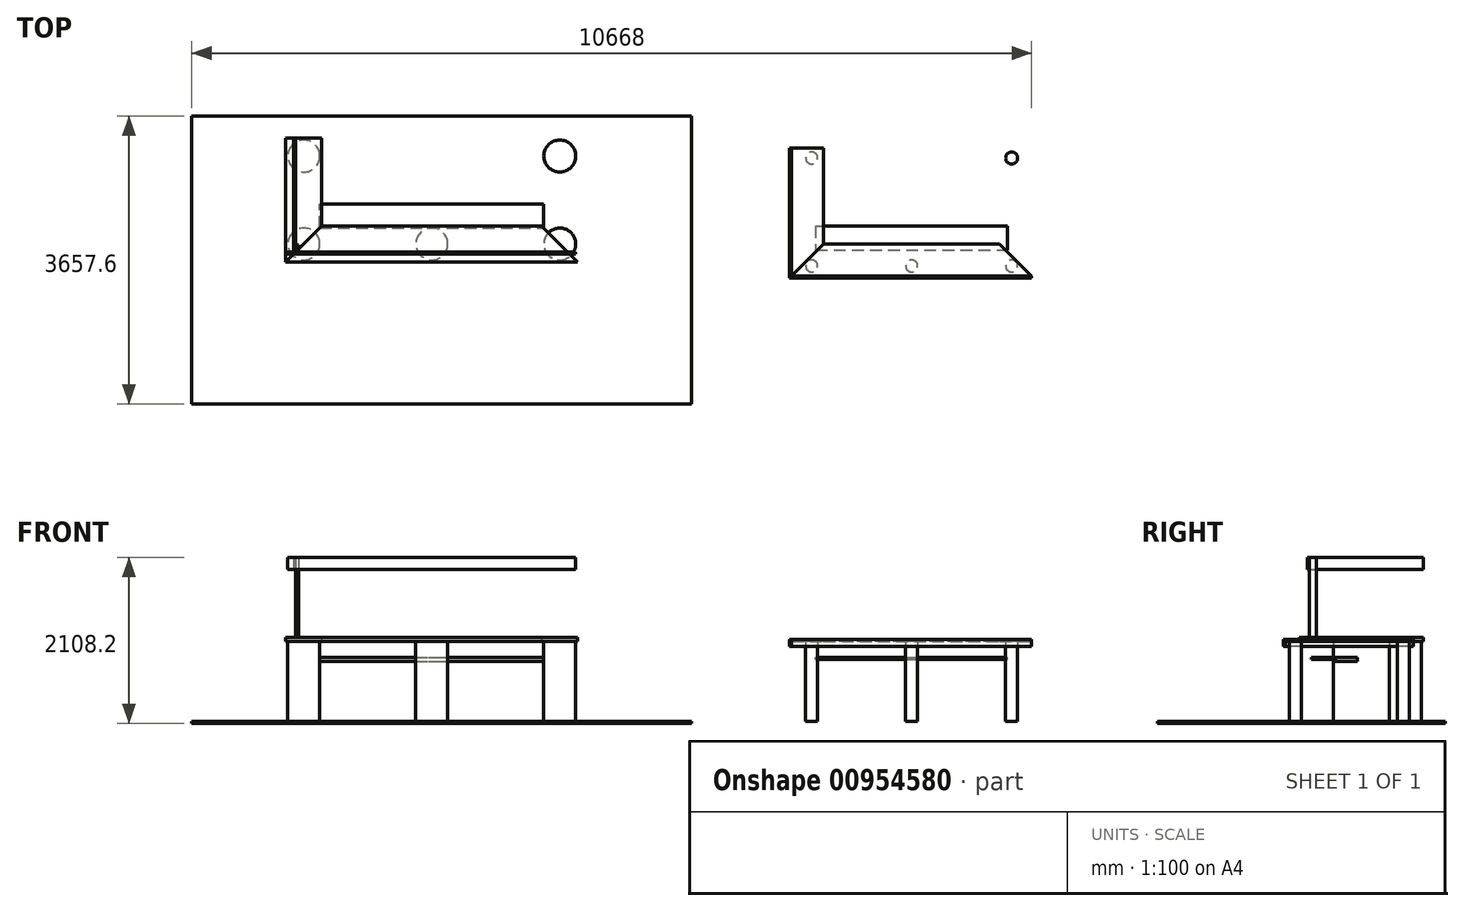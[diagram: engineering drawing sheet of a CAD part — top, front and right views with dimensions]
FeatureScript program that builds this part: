
annotation { "Feature Type Name" : "Feature", "Feature Type Description" : "" }
export const myFeature = defineFeature(function(context is Context, id is Id, definition is map)
    precondition{}
    {
        {
            var Q0;
            Q0=qCreatedBy(makeId("Top.planeOp"),FACE);
            var sketch = newSketch(context, id + "F0", { "sketchPlane" : qUnion([Q0])});
            skLineSegment(sketch, "E0.bottom", {"start": v(-3048, 1828.8) * mm, "end": v(3302, 1828.8) * mm});
            skLineSegment(sketch, "E0.top", {"start": v(-3048, -1828.8) * mm, "end": v(3302, -1828.8) * mm});
            skLineSegment(sketch, "E0.left", {"start": v(-3048, 1828.8) * mm, "end": v(-3048, -1828.8) * mm});
            skLineSegment(sketch, "E0.right", {"start": v(3302, 1828.8) * mm, "end": v(3302, -1828.8) * mm});
            skLineSegment(sketch, "E1", {"start": v(-3048, 0) * mm, "end": v(0, 0) * mm, "construction": true});
            skSolve(sketch);
        }
        {
            var Q0;
            Q0=makeQuery(id+"F0.imprint","IMPRINT",FACE,{"disambiguationData":[TD([[makeQuery(id+"F0.imprint","IMPRINT",EDGE,{"derivedFrom":sQuery(id+"F0.wireOp",EDGE,"E0.bottom")}),-1.0]])]});
            extrude(context, id + "F1", {"entities" : qUnion([Q0]), "oppositeDirection" : true, "depth" : 25.4 * mm, "offsetDistance" : 25.4 * mm});
        }
        {
            var Q0;
            Q0=qCreatedBy(makeId("Top.planeOp"),FACE);
            var sketch = newSketch(context, id + "F2", { "sketchPlane" : qUnion([Q0])});
            skLineSegment(sketch, "E2", {"start": v(0, 0) * mm, "end": v(1625.6, 0) * mm, "construction": true});
            skLineSegment(sketch, "E3", {"start": v(0, 0) * mm, "end": v(-1625.6, 0) * mm, "construction": true});
            skCircle(sketch, "E4", {"center": v(0, 203.2) * mm, "radius": 203.2 * mm});
            skCircle(sketch, "E5", {"center": v(1625.6, 203.2) * mm, "radius": 203.2 * mm});
            skCircle(sketch, "E6", {"center": v(-1625.6, 203.2) * mm, "radius": 203.2 * mm});
            skLineSegment(sketch, "E7", {"start": v(-1625.6, 0) * mm, "end": v(-1625.6, 203.2) * mm, "construction": true});
            skLineSegment(sketch, "E8", {"start": v(0, 203.2) * mm, "end": v(0, 0) * mm, "construction": true});
            skLineSegment(sketch, "E9", {"start": v(1625.6, 203.2) * mm, "end": v(1625.6, 0) * mm, "construction": true});
            skLineSegment(sketch, "E10", {"start": v(-1422.4, 203.2) * mm, "end": v(-203.2, 203.2) * mm, "construction": true});
            skLineSegment(sketch, "E11", {"start": v(203.2, 203.2) * mm, "end": v(1422.4, 203.2) * mm, "construction": true});
            skCircle(sketch, "E12", {"center": v(-1625.6, 1320.8) * mm, "radius": 203.2 * mm});
            skCircle(sketch, "E13", {"center": v(1625.6, 1320.8) * mm, "radius": 203.2 * mm});
            skLineSegment(sketch, "E14", {"start": v(-1625.6, 203.2) * mm, "end": v(-1625.6, 1320.8) * mm, "construction": true});
            skLineSegment(sketch, "E15", {"start": v(1625.6, 203.2) * mm, "end": v(1625.6, 1320.8) * mm, "construction": true});
            skLineSegment(sketch, "E16", {"start": v(-1625.6, 1524) * mm, "end": v(1625.6, 1524) * mm, "construction": true});
            skSolve(sketch);
        }
        {
            var Q0;
            Q0 = qSketchRegion(id + "F2", true);
            extrude(context, id + "F3", {"entities" : qUnion([Q0]), "depth" : 1016 * mm, "offsetDistance" : 25.4 * mm});
        }
        {
            var Q0;
            Q0=qCreatedBy(makeId("Top.planeOp"),FACE);
            cPlane(context, id + "F4", {"entities" : qUnion([Q0]), "cplaneType" : CPlaneType.OFFSET, "offset" : 1016 * mm, "width" : 152.4 * mm, "height" : 152.4 * mm});
        }
        {
            var Q0;
            Q0=qCreatedBy(id+"F4.planeOp",FACE);
            var sketch = newSketch(context, id + "F5", { "sketchPlane" : qUnion([Q0])});
            skLineSegment(sketch, "E17", {"start": v(-1854.2, -25.4) * mm, "end": v(-1397, 431.8) * mm});
            skLineSegment(sketch, "E18", {"start": v(-1397, 431.8) * mm, "end": v(1397, 431.8) * mm});
            skLineSegment(sketch, "E19", {"start": v(1397, 431.8) * mm, "end": v(1854.2, -25.4) * mm});
            skLineSegment(sketch, "E20", {"start": v(1854.2, -25.4) * mm, "end": v(-1854.2, -25.4) * mm});
            skLineSegment(sketch, "E21", {"start": v(0, 0) * mm, "end": v(0, -25.4) * mm, "construction": true});
            skSolve(sketch);
        }
        {
            var Q0;
            Q0=makeQuery(id+"F5.imprint","IMPRINT",FACE,{"disambiguationData":[TD([[makeQuery(id+"F5.imprint","IMPRINT",EDGE,{"derivedFrom":sQuery(id+"F5.wireOp",EDGE,"E17")}),-1.0]])]});
            extrude(context, id + "F6", {"entities" : qUnion([Q0]), "depth" : 50.8 * mm, "offsetDistance" : 25.4 * mm});
        }
        {
            var Q0;
            Q0=qCreatedBy(id+"F4.planeOp",FACE);
            var sketch = newSketch(context, id + "F7", { "sketchPlane" : qUnion([Q0])});
            skLineSegment(sketch, "E22", {"start": v(-1397, 431.8) * mm, "end": v(-1397, 1549.4) * mm});
            skLineSegment(sketch, "E23", {"start": v(-1397, 1549.4) * mm, "end": v(-1854.2, 1549.4) * mm});
            skLineSegment(sketch, "E24", {"start": v(-1854.2, 1549.4) * mm, "end": v(-1854.2, -25.4) * mm});
            skLineSegment(sketch, "E25", {"start": v(-1854.2, -25.4) * mm, "end": v(-1397, 431.8) * mm});
            skLineSegment(sketch, "E26", {"start": v(0, 0) * mm, "end": v(0, -25.4) * mm, "construction": true});
            skLineSegment(sketch, "E27", {"start": v(0, -25.4) * mm, "end": v(-1854.2, -25.4) * mm, "construction": true});
            skSolve(sketch);
        }
        {
            var Q0;
            Q0 = qSketchRegion(id + "F7", true);
            extrude(context, id + "F8", {"entities" : qUnion([Q0]), "depth" : 50.8 * mm, "offsetDistance" : 25.4 * mm});
        }
        {
            var Q0;
            Q0=qCreatedBy(makeId("Top.planeOp"),FACE);
            cPlane(context, id + "F9", {"entities" : qUnion([Q0]), "cplaneType" : CPlaneType.OFFSET, "offset" : 812.8 * mm, "width" : 152.4 * mm, "height" : 152.4 * mm});
        }
        {
            var Q0;
            Q0=qCreatedBy(id+"F9.planeOp",FACE);
            var sketch = newSketch(context, id + "F10", { "sketchPlane" : qUnion([Q0])});
            skLineSegment(sketch, "E28.bottom", {"start": v(-1422.4, 406.4) * mm, "end": v(1422.4, 406.4) * mm});
            skLineSegment(sketch, "E28.top", {"start": v(-1422.4, 711.2) * mm, "end": v(1422.4, 711.2) * mm});
            skLineSegment(sketch, "E28.left", {"start": v(-1422.4, 406.4) * mm, "end": v(-1422.4, 711.2) * mm});
            skLineSegment(sketch, "E28.right", {"start": v(1422.4, 406.4) * mm, "end": v(1422.4, 711.2) * mm});
            skLineSegment(sketch, "E29", {"start": v(0, 0) * mm, "end": v(0, 406.4) * mm, "construction": true});
            skSolve(sketch);
        }
        {
            var Q0;
            Q0 = qSketchRegion(id + "F10", true);
            extrude(context, id + "F11", {"entities" : qUnion([Q0]), "operationType" : NewBodyOperationType.ADD, "oppositeDirection" : true, "depth" : 50.8 * mm, "offsetDistance" : 25.4 * mm});
        }
        {
            var Q0;
            Q0=makeQuery(id+"F6.opExtrude","CAP_FACE",FACE,{"disambiguationData":[OSD([sQuery(id+"F5.wireOp",EDGE,"E17"),sQuery(id+"F5.wireOp",EDGE,"E18"),sQuery(id+"F5.wireOp",EDGE,"E19"),sQuery(id+"F5.wireOp",EDGE,"E20")])],"isStart":false});
            cPlane(context, id + "F12", {"entities" : qUnion([Q0]), "cplaneType" : CPlaneType.OFFSET, "offset" : 0 * mm, "width" : 152.4 * mm, "height" : 152.4 * mm});
        }
        {
            var Q0;
            Q0=qCreatedBy(id+"F12.planeOp",FACE);
            var sketch = newSketch(context, id + "F13", { "sketchPlane" : qUnion([Q0])});
            skLineSegment(sketch, "E30.bottom", {"start": v(-1727.2, 190.5) * mm, "end": v(-1689.1, 190.5) * mm});
            skLineSegment(sketch, "E30.top", {"start": v(-1727.2, 101.6) * mm, "end": v(-1689.1, 101.6) * mm});
            skLineSegment(sketch, "E30.left", {"start": v(-1727.2, 190.5) * mm, "end": v(-1727.2, 101.6) * mm});
            skLineSegment(sketch, "E30.right", {"start": v(-1689.1, 190.5) * mm, "end": v(-1689.1, 101.6) * mm});
            skLineSegment(sketch, "E31", {"start": v(0, 0) * mm, "end": v(-1727.2, 0) * mm, "construction": true});
            skLineSegment(sketch, "E32", {"start": v(-1727.2, 0) * mm, "end": v(-1727.2, 101.6) * mm, "construction": true});
            skSolve(sketch);
        }
        {
            var Q0;
            Q0 = qSketchRegion(id + "F13", true);
            extrude(context, id + "F14", {"entities" : qUnion([Q0]), "depth" : 1016 * mm, "offsetDistance" : 25.4 * mm});
        }
        {
            var Q0;
            Q0=makeQuery(id+"F14.opExtrude","SWEPT_FACE",FACE,{"disambiguationData":[OSD([sQuery(id+"F13.wireOp",EDGE,"E30.top")])]});
            var sketch = newSketch(context, id + "F15", { "sketchPlane" : qUnion([Q0])});
            skLineSegment(sketch, "E33.bottom", {"start": v(-1828.8, 2082.8) * mm, "end": v(1828.8, 2082.8) * mm});
            skLineSegment(sketch, "E33.top", {"start": v(-1828.8, 1930.4) * mm, "end": v(1828.8, 1930.4) * mm});
            skLineSegment(sketch, "E33.left", {"start": v(-1828.8, 2082.8) * mm, "end": v(-1828.8, 1930.4) * mm});
            skLineSegment(sketch, "E33.right", {"start": v(1828.8, 2082.8) * mm, "end": v(1828.8, 1930.4) * mm});
            skLineSegment(sketch, "E34", {"start": v(0, 0) * mm, "end": v(0, 1930.4) * mm, "construction": true});
            skSolve(sketch);
        }
        {
            var Q0;
            Q0 = qSketchRegion(id + "F15", true);
            extrude(context, id + "F16", {"entities" : qUnion([Q0]), "depth" : 25.4 * mm, "offsetDistance" : 25.4 * mm});
        }
        {
            var Q0;
            Q0=makeQuery(id+"F14.opExtrude","SWEPT_FACE",FACE,{"disambiguationData":[OSD([sQuery(id+"F13.wireOp",EDGE,"E30.left")])]});
            var sketch = newSketch(context, id + "F17", { "sketchPlane" : qUnion([Q0])});
            skLineSegment(sketch, "E35.bottom", {"start": v(-101.6, 2082.8) * mm, "end": v(-1549.4, 2082.8) * mm});
            skLineSegment(sketch, "E35.top", {"start": v(-101.6, 1930.4) * mm, "end": v(-1549.4, 1930.4) * mm});
            skLineSegment(sketch, "E35.left", {"start": v(-101.6, 2082.8) * mm, "end": v(-101.6, 1930.4) * mm});
            skLineSegment(sketch, "E35.right", {"start": v(-1549.4, 2082.8) * mm, "end": v(-1549.4, 1930.4) * mm});
            skSolve(sketch);
        }
        {
            var Q0;
            Q0 = qSketchRegion(id + "F17", true);
            extrude(context, id + "F18", {"entities" : qUnion([Q0]), "depth" : 25.4 * mm, "offsetDistance" : 25.4 * mm});
        }
        {
            var Q0;
            Q0=qCreatedBy(makeId("Top.planeOp"),FACE);
            var sketch = newSketch(context, id + "F19", { "sketchPlane" : qUnion([Q0])});
            skLineSegment(sketch, "E36", {"start": v(4902.2, 1295.4) * mm, "end": v(4902.2, 0) * mm, "construction": true});
            skLineSegment(sketch, "E37", {"start": v(4902.2, 0) * mm, "end": v(7289.8, 0) * mm, "construction": true});
            skLineSegment(sketch, "E38", {"start": v(7289.8, 0) * mm, "end": v(7289.8, 1295.4) * mm, "construction": true});
            skLineSegment(sketch, "E39", {"start": v(6096, 0) * mm, "end": v(6096, 660.28) * mm, "construction": true});
            skCircle(sketch, "E40", {"center": v(6096, -76.2) * mm, "radius": 76.2 * mm});
            skCircle(sketch, "E41", {"center": v(4826, -76.2) * mm, "radius": 76.2 * mm});
            skCircle(sketch, "E42", {"center": v(7366, -76.2) * mm, "radius": 76.2 * mm});
            skCircle(sketch, "E43", {"center": v(4826, 1295.4) * mm, "radius": 76.2 * mm});
            skCircle(sketch, "E44", {"center": v(7366, 1295.4) * mm, "radius": 76.2 * mm});
            skLineSegment(sketch, "E45", {"start": v(4826, 1295.4) * mm, "end": v(4826, -76.2) * mm, "construction": true});
            skLineSegment(sketch, "E46", {"start": v(6096, -76.2) * mm, "end": v(4826, -76.2) * mm, "construction": true});
            skLineSegment(sketch, "E47", {"start": v(6096, -76.2) * mm, "end": v(7366, -76.2) * mm, "construction": true});
            skLineSegment(sketch, "E48", {"start": v(7366, -76.2) * mm, "end": v(7366, 1295.4) * mm, "construction": true});
            skLineSegment(sketch, "E49", {"start": v(4826, 1295.4) * mm, "end": v(4902.2, 1295.4) * mm, "construction": true});
            skLineSegment(sketch, "E50", {"start": v(7289.8, 1295.4) * mm, "end": v(7366, 1295.4) * mm, "construction": true});
            skSolve(sketch);
        }
        {
            var Q0;
            Q0 = qSketchRegion(id + "F19", true);
            extrude(context, id + "F20", {"entities" : qUnion([Q0]), "depth" : 1016 * mm, "offsetDistance" : 25.4 * mm});
        }
        {
            var Q0;
            Q0=qCreatedBy(id+"F4.planeOp",FACE);
            var sketch = newSketch(context, id + "F21", { "sketchPlane" : qUnion([Q0])});
            skLineSegment(sketch, "E51", {"start": v(4572, -203.2) * mm, "end": v(4978.4, 203.2) * mm});
            skLineSegment(sketch, "E52", {"start": v(4978.4, 203.2) * mm, "end": v(7213.6, 203.2) * mm});
            skLineSegment(sketch, "E53", {"start": v(7213.6, 203.2) * mm, "end": v(7620, -203.2) * mm});
            skLineSegment(sketch, "E54", {"start": v(7620, -203.2) * mm, "end": v(4572, -203.2) * mm});
            skLineSegment(sketch, "E55", {"start": v(0, 0) * mm, "end": v(6096, 0) * mm, "construction": true});
            skLineSegment(sketch, "E56", {"start": v(6096, 0) * mm, "end": v(6096, -203.2) * mm, "construction": true});
            skSolve(sketch);
        }
        {
            var Q0;
            Q0 = qSketchRegion(id + "F21", true);
            extrude(context, id + "F22", {"entities" : qUnion([Q0]), "depth" : 25.4 * mm, "offsetDistance" : 25.4 * mm});
        }
        {
            var Q0;
            Q0=qCreatedBy(id+"F9.planeOp",FACE);
            var sketch = newSketch(context, id + "F23", { "sketchPlane" : qUnion([Q0])});
            skLineSegment(sketch, "E57.bottom", {"start": v(4876.8, 431.8) * mm, "end": v(7315.2, 431.8) * mm});
            skLineSegment(sketch, "E57.top", {"start": v(4876.8, 127) * mm, "end": v(7315.2, 127) * mm});
            skLineSegment(sketch, "E57.left", {"start": v(4876.8, 431.8) * mm, "end": v(4876.8, 127) * mm});
            skLineSegment(sketch, "E57.right", {"start": v(7315.2, 431.8) * mm, "end": v(7315.2, 127) * mm});
            skLineSegment(sketch, "E58", {"start": v(0, 0) * mm, "end": v(6096, 0) * mm, "construction": true});
            skLineSegment(sketch, "E59", {"start": v(6096, 0) * mm, "end": v(6096, 127) * mm, "construction": true});
            skSolve(sketch);
        }
        {
            var Q0;
            Q0 = qSketchRegion(id + "F23", true);
            extrude(context, id + "F24", {"entities" : qUnion([Q0]), "oppositeDirection" : true, "depth" : 25.4 * mm, "offsetDistance" : 25.4 * mm});
        }
        {
            var Q0;
            Q0=makeQuery(id+"F22.opExtrude","SWEPT_FACE",FACE,{"disambiguationData":[OSD([sQuery(id+"F21.wireOp",EDGE,"E54")])]});
            var sketch = newSketch(context, id + "F25", { "sketchPlane" : qUnion([Q0])});
            skLineSegment(sketch, "E60.bottom", {"start": v(4572, 1041.4) * mm, "end": v(7620, 1041.4) * mm});
            skLineSegment(sketch, "E60.top", {"start": v(4572, 952.5) * mm, "end": v(7620, 952.5) * mm});
            skLineSegment(sketch, "E60.left", {"start": v(4572, 1041.4) * mm, "end": v(4572, 952.5) * mm});
            skLineSegment(sketch, "E60.right", {"start": v(7620, 1041.4) * mm, "end": v(7620, 952.5) * mm});
            skSolve(sketch);
        }
        {
            var Q0;
            Q0 = qSketchRegion(id + "F25", true);
            extrude(context, id + "F26", {"entities" : qUnion([Q0]), "depth" : 25.4 * mm, "offsetDistance" : 25.4 * mm});
        }
        {
            var Q0;
            Q0=makeQuery(id+"F22.opExtrude","CAP_FACE",FACE,{"disambiguationData":[OSD([sQuery(id+"F21.wireOp",EDGE,"E51"),sQuery(id+"F21.wireOp",EDGE,"E52"),sQuery(id+"F21.wireOp",EDGE,"E53"),sQuery(id+"F21.wireOp",EDGE,"E54")])],"isStart":false});
            var sketch = newSketch(context, id + "F27", { "sketchPlane" : qUnion([Q0])});
            skLineSegment(sketch, "E61", {"start": v(4978.4, 203.2) * mm, "end": v(4978.4, 1422.4) * mm});
            skLineSegment(sketch, "E62", {"start": v(4978.4, 1422.4) * mm, "end": v(4572, 1422.4) * mm});
            skLineSegment(sketch, "E63", {"start": v(4572, 1422.4) * mm, "end": v(4572, -203.2) * mm});
            skSolve(sketch);
        }
        {
            var Q0;
            Q0 = qSketchRegion(id + "F27", true);
            var Q1;
            Q1=makeQuery(id+"F27.imprint","IMPRINT",FACE,{"disambiguationData":[TD([[makeQuery(id+"F27.imprint","IMPRINT",EDGE,{"derivedFrom":sQuery(id+"F27.wireOp",EDGE,"E61")}),1.0]])]});
            extrude(context, id + "F28", {"entities" : qUnion([Q0, Q1]), "oppositeDirection" : true, "depth" : 25.4 * mm, "offsetDistance" : 25.4 * mm});
        }
        {
            var Q0;
            Q0=makeQuery(id+"F28.opExtrude","SWEPT_FACE",FACE,{"disambiguationData":[OSD([sQuery(id+"F27.wireOp",EDGE,"E63")])]});
            var sketch = newSketch(context, id + "F29", { "sketchPlane" : qUnion([Q0])});
            skLineSegment(sketch, "E64.bottom", {"start": v(-1422.4, 1041.4) * mm, "end": v(228.6, 1041.4) * mm});
            skLineSegment(sketch, "E64.top", {"start": v(-1422.4, 952.5) * mm, "end": v(228.6, 952.5) * mm});
            skLineSegment(sketch, "E64.left", {"start": v(-1422.4, 1041.4) * mm, "end": v(-1422.4, 952.5) * mm});
            skLineSegment(sketch, "E64.right", {"start": v(228.6, 1041.4) * mm, "end": v(228.6, 952.5) * mm});
            skSolve(sketch);
        }
        {
            var Q0;
            Q0 = qSketchRegion(id + "F29", true);
            extrude(context, id + "F30", {"entities" : qUnion([Q0]), "depth" : 25.4 * mm, "offsetDistance" : 25.4 * mm});
        }
    });
